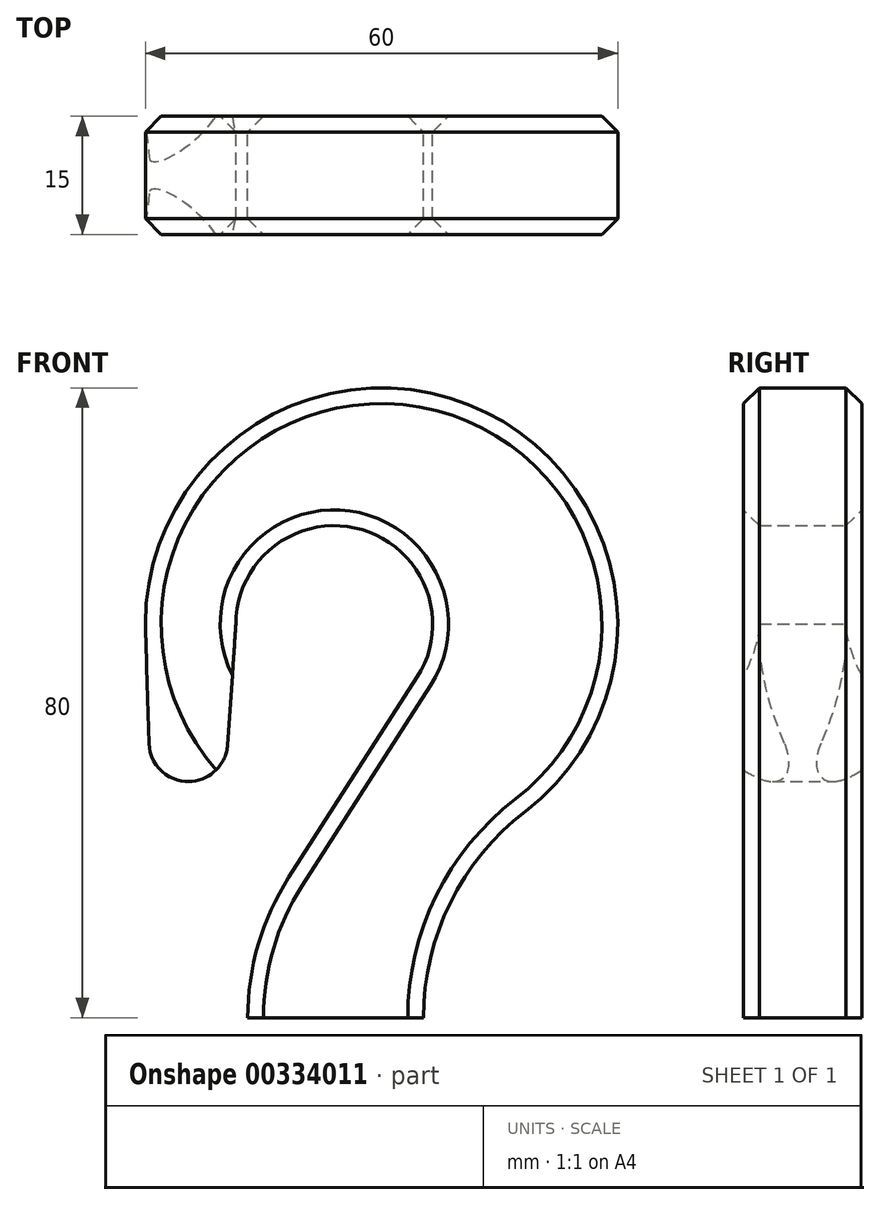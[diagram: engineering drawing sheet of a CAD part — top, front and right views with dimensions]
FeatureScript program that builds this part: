
annotation { "Feature Type Name" : "Feature", "Feature Type Description" : "" }
export const myFeature = defineFeature(function(context is Context, id is Id, definition is map)
    precondition{}
    {
        {
            var Q0;
            Q0=qCreatedBy(makeId("Front.planeOp"),FACE);
            var sketch = newSketch(context, id + "F0", { "sketchPlane" : qUnion([Q0])});
            skArc(sketch, "E0", {"start": v(-5.78, 17.8) * mm, "mid": v(-9.67, 9.28) * mm, "end": v(-11, 0) * mm});
            skArc(sketch, "E1", {"start": v(24.25, 26.19) * mm, "mid": v(14.74, 14.6) * mm, "end": v(11.33, 0) * mm});
            skLineSegment(sketch, "E2", {"start": v(0, 56.14) * mm, "end": v(0, -51.85) * mm, "construction": true});
            skArc(sketch, "E3", {"start": v(10.52, 43.26) * mm, "mid": v(3.51, 62) * mm, "end": v(-12.5, 50) * mm});
            skArc(sketch, "E4", {"start": v(24.25, 26.19) * mm, "mid": v(19.28, 76.9) * mm, "end": v(-24, 50) * mm});
            skLineSegment(sketch, "E5", {"start": v(10.52, 43.26) * mm, "end": v(-5.78, 17.8) * mm});
            skLineSegment(sketch, "E6", {"start": v(-58.75, 0) * mm, "end": v(71.28, 0) * mm, "construction": true});
            skLineSegment(sketch, "E7", {"start": v(0, 50) * mm, "end": v(-36.09, 50) * mm, "construction": true});
            skLineSegment(sketch, "E8", {"start": v(-24, 50) * mm, "end": v(-12.5, 50) * mm});
            skArc(sketch, "E9", {"start": v(-23.54, 34.85) * mm, "mid": v(-18.64, 30) * mm, "end": v(-13.56, 34.66) * mm});
            skLineSegment(sketch, "E10", {"start": v(-24, 50) * mm, "end": v(-23.54, 34.85) * mm});
            skLineSegment(sketch, "E11", {"start": v(-12.5, 50) * mm, "end": v(-13.56, 34.66) * mm});
            skLineSegment(sketch, "E12", {"start": v(-11, 0) * mm, "end": v(11.33, 0) * mm});
            skSolve(sketch);
        }
        {
            var Q0;
            Q0 = qSketchRegion(id + "F0", true);
            var Q1;
            Q1=makeQuery(id+"F0.imprint","IMPRINT",FACE,{"disambiguationData":[TD([[makeQuery(id+"F0.imprint","IMPRINT",EDGE,{"derivedFrom":sQuery(id+"F0.wireOp",EDGE,"E0")}),1.0]])]});
            var Q2;
            Q2=makeQuery(id+"F0.imprint","IMPRINT",FACE,{"disambiguationData":[TD([[makeQuery(id+"F0.imprint","IMPRINT",EDGE,{"derivedFrom":sQuery(id+"F0.wireOp",EDGE,"E8")}),-1.0]])]});
            extrude(context, id + "F1", {"entities" : qUnion([Q0, Q1, Q2]), "endBound" : BoundingType.SYMMETRIC, "depth" : 15 * mm});
        }
        {
            var Q0;
            Q0=makeQuery(id+"F1.opExtrude","CAP_EDGE",EDGE,{"disambiguationData":[OSD([sQuery(id+"F0.wireOp",EDGE,"E4")])],"isStart":false});
            var Q1;
            Q1=makeQuery(id+"F1.opExtrude","CAP_EDGE",EDGE,{"disambiguationData":[OSD([sQuery(id+"F0.wireOp",EDGE,"E4")])],"isStart":true});
            chamfer(context, id + "F2", {"entities" : qUnion([Q0, Q1]), "width" : 2 * mm, "tangentPropagation" : true});
        }
        {
            var Q0;
            Q0=makeQuery(id+"F1.opExtrude","CAP_EDGE",EDGE,{"disambiguationData":[OSD([sQuery(id+"F0.wireOp",EDGE,"E5")])],"isStart":false});
            var Q1;
            Q1=makeQuery(id+"F1.opExtrude","CAP_EDGE",EDGE,{"disambiguationData":[OSD([sQuery(id+"F0.wireOp",EDGE,"E3")])],"isStart":true});
            chamfer(context, id + "F3", {"entities" : qUnion([Q0, Q1]), "width" : 2 * mm, "tangentPropagation" : true});
        }
    });
